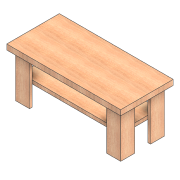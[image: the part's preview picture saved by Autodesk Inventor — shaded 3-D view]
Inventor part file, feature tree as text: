
AUTODESK INVENTOR PART (.ipt)
format: ipt  version: 2020.2 (Build 242310000, 310)  size: 194,048 bytes
history: native  units: mm
features: extrude x3, sketch x3, plane x2
ambient origin geometry x8: Origin, YZ Plane, XZ Plane, XY Plane, X Axis, Y Axis, Z Axis, Center Point
bodies: Solid1 (feature_tree)
feature tree (8):
  extrude  "Extrusion1"  Depth=600.0mm
  plane  "Work Plane1"
  extrude  "Extrusion2"  Depth=160.0mm
  plane  "Work Plane2"
  extrude  "Extrusion3"  Depth=50.0mm
  sketch  "Sketch1"  dims[d0=1300.0mm d1=600.0mm]
  sketch  "Sketch2"  dims[d4=30.0mm d5=160.0mm]
  sketch  "Sketch3"  dims[d6=30.0mm d7=50.0mm d8=50.0mm d9=50.0mm d10=50.0mm d11=30.0mm d12=160.0mm d13=160.0mm d14=30.0mm d15=60.0mm d16=0.0mm d17=0.0mm d18=50.0mm d19=50.0mm d20=50.0mm d21=50.0mm d22=50.0mm d23=50.0mm d24=50.0mm d25=50.0mm d26=160.0mm d27=30.0mm d28=30.0mm d29=160.0mm d30=160.0mm d31=30.0mm d32=30.0mm d33=160.0mm d34=160.0mm d35=30.0mm d36=30.0mm d37=160.0mm d38=500.0mm d39=0.0mm d40=250.0mm d41=20.0mm d42=20.0mm d43=0.0mm d44=0.0mm]
